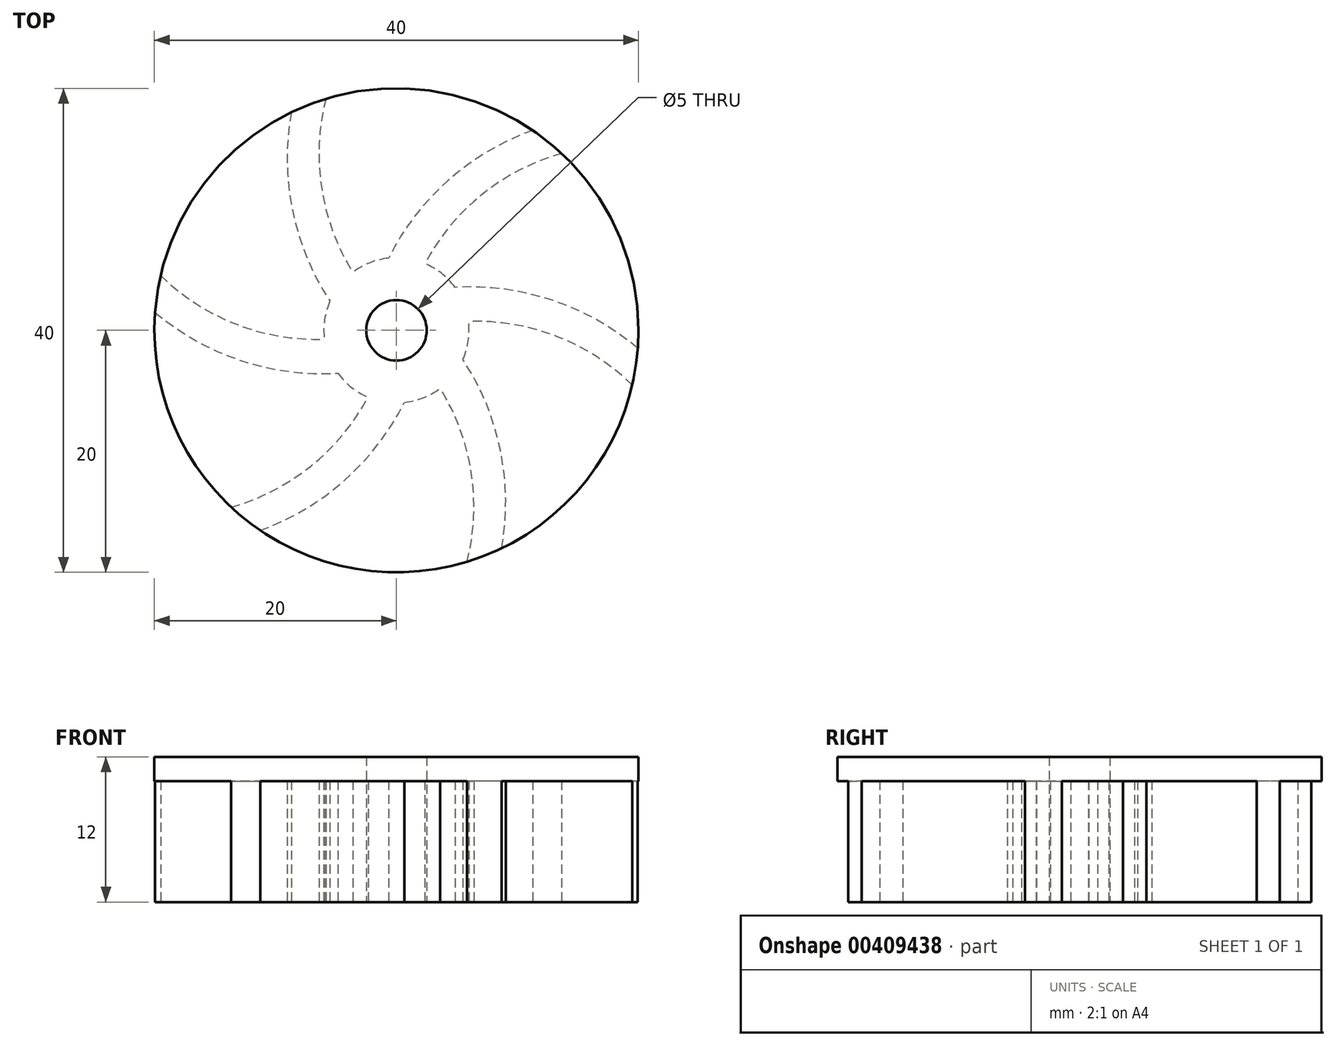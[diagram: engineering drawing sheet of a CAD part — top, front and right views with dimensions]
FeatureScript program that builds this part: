
annotation { "Feature Type Name" : "Feature", "Feature Type Description" : "" }
export const myFeature = defineFeature(function(context is Context, id is Id, definition is map)
    precondition{}
    {
        {
            var Q0;
            Q0=qCreatedBy(makeId("Top.planeOp"),FACE);
            var sketch = newSketch(context, id + "F0", { "sketchPlane" : qUnion([Q0])});
            skArc(sketch, "E0", {"start": v(13.66, 14.61) * mm, "mid": v(12.5, 15.62) * mm, "end": v(11.25, 16.53) * mm});
            skArc(sketch, "E1.0", {"start": v(11.25, 16.53) * mm, "mid": v(4.28, 12.4) * mm, "end": v(-0.66, 5.96) * mm});
            skArc(sketch, "E2.0", {"start": v(13.66, 14.61) * mm, "mid": v(7.07, 11.22) * mm, "end": v(2.34, 5.52) * mm});
            skPoint(sketch, "E3.center.orphan", {"position": v(20, 0) * mm});
            skArc(sketch, "E4", {"start": v(-5.5, 2.41) * mm, "mid": v(-5.94, 0.87) * mm, "end": v(-5.96, -0.73) * mm});
            skPoint(sketch, "E5.orphan", {"position": v(-1.5, 0) * mm});
            skPoint(sketch, "E6.orphan", {"position": v(-0.75, 1.3) * mm});
            skPoint(sketch, "E7.orphan", {"position": v(0.75, 1.3) * mm});
            skPoint(sketch, "E8.orphan", {"position": v(-0.75, -1.3) * mm});
            skPoint(sketch, "E9.orphan", {"position": v(0.75, -1.3) * mm});
            skArc(sketch, "E10.trimOffspring", {"start": v(-0.66, 5.96) * mm, "mid": v(-2.21, 5.58) * mm, "end": v(-3.61, 4.8) * mm});
            skArc(sketch, "E11.trimOffspring", {"start": v(4.84, 3.55) * mm, "mid": v(3.72, 4.7) * mm, "end": v(2.34, 5.52) * mm});
            skArc(sketch, "E12.trimOffspring", {"start": v(5.5, -2.41) * mm, "mid": v(5.94, -0.87) * mm, "end": v(5.96, 0.73) * mm});
            skArc(sketch, "E13.trimOffspring", {"start": v(0.66, -5.96) * mm, "mid": v(2.21, -5.58) * mm, "end": v(3.61, -4.8) * mm});
            skArc(sketch, "E14.trimOffspring", {"start": v(-4.84, -3.55) * mm, "mid": v(-3.72, -4.7) * mm, "end": v(-2.34, -5.52) * mm});
            skCircle(sketch, "E15", {"center": v(0, 0) * mm, "radius": 2.5 * mm});
            skArc(sketch, "E16.1.0", {"start": v(19.95, -1.48) * mm, "mid": v(12.87, 2.49) * mm, "end": v(4.84, 3.55) * mm});
            skArc(sketch, "E16.1.1", {"start": v(19.48, -4.52) * mm, "mid": v(13.26, -0.51) * mm, "end": v(5.96, 0.73) * mm});
            skArc(sketch, "E16.1.2", {"start": v(19.48, -4.52) * mm, "mid": v(19.77, -3) * mm, "end": v(19.95, -1.48) * mm});
            skArc(sketch, "E16.2.0", {"start": v(8.7, -18.01) * mm, "mid": v(8.59, -9.9) * mm, "end": v(5.5, -2.41) * mm});
            skArc(sketch, "E16.2.1", {"start": v(5.83, -19.13) * mm, "mid": v(6.18, -11.74) * mm, "end": v(3.61, -4.8) * mm});
            skArc(sketch, "E16.2.2", {"start": v(5.83, -19.13) * mm, "mid": v(7.28, -18.63) * mm, "end": v(8.7, -18.01) * mm});
            skArc(sketch, "E16.3.0", {"start": v(-11.25, -16.53) * mm, "mid": v(-4.28, -12.4) * mm, "end": v(0.66, -5.96) * mm});
            skArc(sketch, "E16.3.1", {"start": v(-13.65, -14.61) * mm, "mid": v(-7.07, -11.22) * mm, "end": v(-2.34, -5.52) * mm});
            skArc(sketch, "E16.3.2", {"start": v(-13.65, -14.61) * mm, "mid": v(-12.5, -15.62) * mm, "end": v(-11.25, -16.53) * mm});
            skArc(sketch, "E16.4.0", {"start": v(-19.95, 1.48) * mm, "mid": v(-12.87, -2.49) * mm, "end": v(-4.84, -3.55) * mm});
            skArc(sketch, "E16.4.1", {"start": v(-19.48, 4.52) * mm, "mid": v(-13.26, 0.51) * mm, "end": v(-5.96, -0.73) * mm});
            skArc(sketch, "E16.4.2", {"start": v(-19.48, 4.52) * mm, "mid": v(-19.77, 3) * mm, "end": v(-19.95, 1.48) * mm});
            skArc(sketch, "E16.5.0", {"start": v(-8.7, 18.01) * mm, "mid": v(-8.59, 9.9) * mm, "end": v(-5.5, 2.41) * mm});
            skArc(sketch, "E16.5.1", {"start": v(-5.83, 19.13) * mm, "mid": v(-6.18, 11.74) * mm, "end": v(-3.61, 4.8) * mm});
            skArc(sketch, "E16.5.2", {"start": v(-5.83, 19.13) * mm, "mid": v(-7.28, 18.63) * mm, "end": v(-8.7, 18.01) * mm});
            skLineSegment(sketch, "E16.anchor1", {"start": v(0, 0) * mm, "end": v(-0.66, 5.96) * mm, "construction": true});
            skLineSegment(sketch, "E16.anchor2", {"start": v(0, 0) * mm, "end": v(-5.5, 2.41) * mm, "construction": true});
            skPoint(sketch, "E17.orphan", {"position": v(7.28, -23.92) * mm});
            skPoint(sketch, "E18.orphan", {"position": v(24.35, -5.65) * mm});
            skSolve(sketch);
        }
        {
            var Q0;
            Q0=qSketchRegion(id+"F0",true);
            extrude(context, id + "F1", {"entities" : qUnion([Q0]), "depth" : 12 * mm, "offsetDistance" : 25 * mm});
        }
        {
            var Q0;
            Q0=makeQuery(id+"F1.opExtrude","CAP_FACE",FACE,{"disambiguationData":[OSD([sQuery(id+"F0.wireOp",EDGE,"E0"),sQuery(id+"F0.wireOp",EDGE,"E1.0"),sQuery(id+"F0.wireOp",EDGE,"E2.0"),sQuery(id+"F0.wireOp",EDGE,"d8a1bce4-6bac-4e10-b3d6-3fa7cdfdab0b.1.0"),sQuery(id+"F0.wireOp",EDGE,"d8a1bce4-6bac-4e10-b3d6-3fa7cdfdab0b.1.1"),sQuery(id+"F0.wireOp",EDGE,"d8a1bce4-6bac-4e10-b3d6-3fa7cdfdab0b.1.2"),sQuery(id+"F0.wireOp",EDGE,"d8a1bce4-6bac-4e10-b3d6-3fa7cdfdab0b.2.0"),sQuery(id+"F0.wireOp",EDGE,"d8a1bce4-6bac-4e10-b3d6-3fa7cdfdab0b.2.1"),sQuery(id+"F0.wireOp",EDGE,"d8a1bce4-6bac-4e10-b3d6-3fa7cdfdab0b.2.2"),sQuery(id+"F0.wireOp",EDGE,"d8a1bce4-6bac-4e10-b3d6-3fa7cdfdab0b.3.0"),sQuery(id+"F0.wireOp",EDGE,"d8a1bce4-6bac-4e10-b3d6-3fa7cdfdab0b.3.1"),sQuery(id+"F0.wireOp",EDGE,"d8a1bce4-6bac-4e10-b3d6-3fa7cdfdab0b.3.2"),sQuery(id+"F0.wireOp",EDGE,"d8a1bce4-6bac-4e10-b3d6-3fa7cdfdab0b.4.0"),sQuery(id+"F0.wireOp",EDGE,"d8a1bce4-6bac-4e10-b3d6-3fa7cdfdab0b.4.1"),sQuery(id+"F0.wireOp",EDGE,"d8a1bce4-6bac-4e10-b3d6-3fa7cdfdab0b.4.2"),sQuery(id+"F0.wireOp",EDGE,"d8a1bce4-6bac-4e10-b3d6-3fa7cdfdab0b.5.0"),sQuery(id+"F0.wireOp",EDGE,"d8a1bce4-6bac-4e10-b3d6-3fa7cdfdab0b.5.1"),sQuery(id+"F0.wireOp",EDGE,"d8a1bce4-6bac-4e10-b3d6-3fa7cdfdab0b.5.2"),sQuery(id+"F0.wireOp",EDGE,"E4"),sQuery(id+"F0.wireOp",EDGE,"E10.trimOffspring"),sQuery(id+"F0.wireOp",EDGE,"E11.trimOffspring"),sQuery(id+"F0.wireOp",EDGE,"E12.trimOffspring"),sQuery(id+"F0.wireOp",EDGE,"E13.trimOffspring"),sQuery(id+"F0.wireOp",EDGE,"E14.trimOffspring"),sQuery(id+"F0.wireOp",EDGE,"E15")])],"isStart":false});
            var sketch = newSketch(context, id + "F2", { "sketchPlane" : qUnion([Q0])});
            skCircle(sketch, "E19", {"center": v(0, 0) * mm, "radius": 20 * mm});
            skCircle(sketch, "E20", {"center": v(0, 0) * mm, "radius": 2.5 * mm});
            skSolve(sketch);
        }
        {
            var Q0;
            Q0 = qSketchRegion(id + "F2", true);
            extrude(context, id + "F3", {"entities" : qUnion([Q0]), "operationType" : NewBodyOperationType.ADD, "oppositeDirection" : true, "depth" : 2 * mm, "offsetDistance" : 25 * mm});
        }
    });
